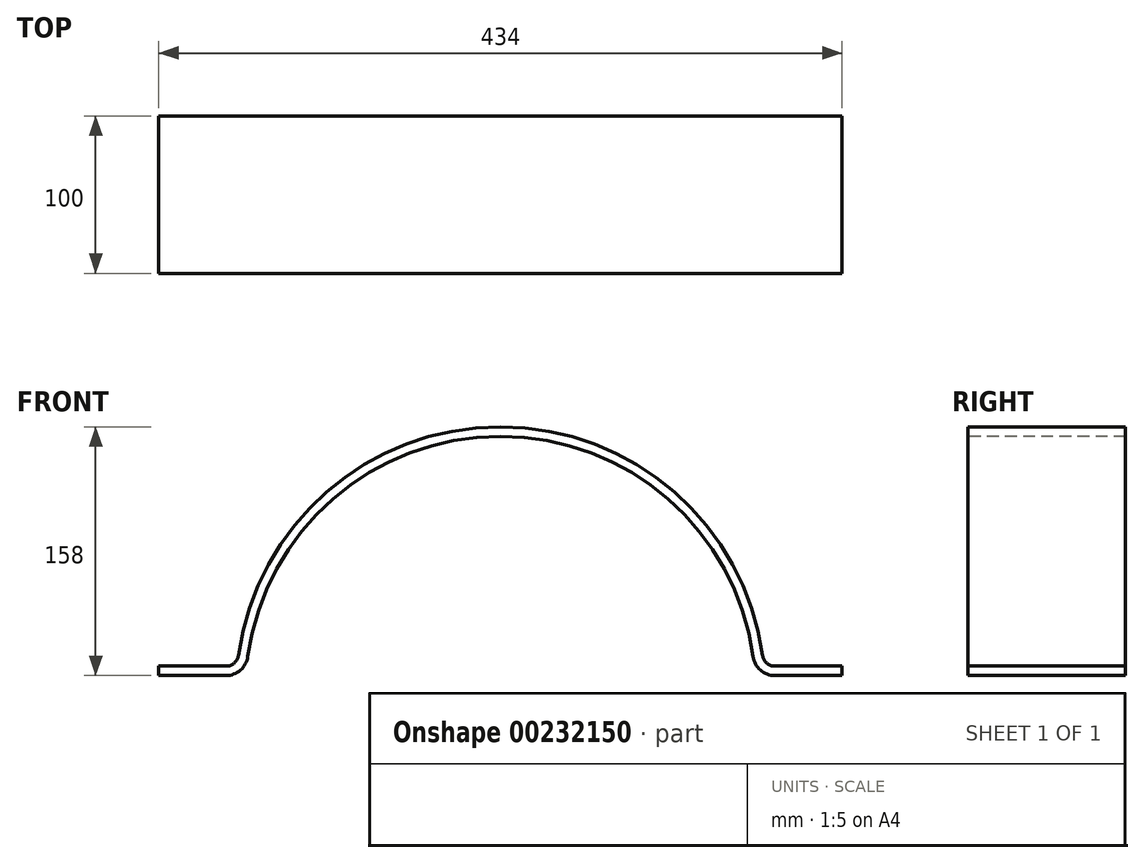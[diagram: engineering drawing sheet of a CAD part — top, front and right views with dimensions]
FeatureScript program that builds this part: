
annotation { "Feature Type Name" : "Feature", "Feature Type Description" : "" }
export const myFeature = defineFeature(function(context is Context, id is Id, definition is map)
    precondition{}
    {
        {
            var Q0;
            Q0=qCreatedBy(makeId("Front.planeOp"),FACE);
            var sketch = newSketch(context, id + "F0", { "sketchPlane" : qUnion([Q0])});
            skArc(sketch, "E0", {"start": v(174.9, 5.23) * mm, "mid": v(14.42, 145.14) * mm, "end": v(-146.07, 5.23) * mm});
            skArc(sketch, "E1.0", {"start": v(180.85, 6.05) * mm, "mid": v(14.42, 151.14) * mm, "end": v(-152.01, 6.05) * mm});
            skLineSegment(sketch, "E2.0", {"start": v(-202.58, -6.86) * mm, "end": v(-159.94, -6.86) * mm});
            skLineSegment(sketch, "E3.0", {"start": v(-202.58, -0.86) * mm, "end": v(-159.94, -0.86) * mm});
            skLineSegment(sketch, "E4", {"start": v(14.42, -16.86) * mm, "end": v(14.42, -240.67) * mm, "construction": true});
            skLineSegment(sketch, "E5.0", {"start": v(-202.58, -0.86) * mm, "end": v(-202.58, -6.86) * mm});
            skLineSegment(sketch, "E6.0", {"start": v(231.42, -0.86) * mm, "end": v(231.42, -6.86) * mm});
            skPoint(sketch, "E7.orphan", {"position": v(-245.11, -16.86) * mm});
            skLineSegment(sketch, "E8.trimOffspring", {"start": v(188.77, -0.86) * mm, "end": v(231.42, -0.86) * mm});
            skLineSegment(sketch, "E9.trimOffspring", {"start": v(188.77, -6.86) * mm, "end": v(231.42, -6.86) * mm});
            skPoint(sketch, "E10.visualSharp", {"position": v(-147.27, -6.86) * mm});
            skArc(sketch, "E10.filletArc", {"start": v(-159.94, -6.86) * mm, "mid": v(-150.74, -3.41) * mm, "end": v(-146.07, 5.23) * mm});
            skPoint(sketch, "E11.visualSharp", {"position": v(176.1, -6.86) * mm});
            skArc(sketch, "E11.filletArc", {"start": v(174.9, 5.23) * mm, "mid": v(179.57, -3.41) * mm, "end": v(188.77, -6.86) * mm});
            skPoint(sketch, "E12.visualSharp", {"position": v(181.65, -0.86) * mm});
            skArc(sketch, "E12.filletArc", {"start": v(180.85, 6.05) * mm, "mid": v(183.52, 1.1) * mm, "end": v(188.77, -0.86) * mm});
            skPoint(sketch, "E13.visualSharp", {"position": v(-152.82, -0.86) * mm});
            skArc(sketch, "E13.filletArc", {"start": v(-159.94, -0.86) * mm, "mid": v(-154.68, 1.1) * mm, "end": v(-152.01, 6.05) * mm});
            skSolve(sketch);
        }
        {
            var Q0;
            Q0=makeQuery(id+"F0.imprint","IMPRINT",FACE,{"disambiguationData":[TD([[makeQuery(id+"F0.imprint","IMPRINT",EDGE,{"derivedFrom":sQuery(id+"F0.wireOp",EDGE,"E0")}),-1.0]])]});
            extrude(context, id + "F1", {"entities" : qUnion([Q0]), "oppositeDirection" : true, "depth" : 100 * mm});
        }
    });
